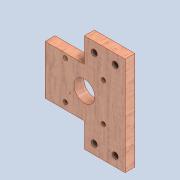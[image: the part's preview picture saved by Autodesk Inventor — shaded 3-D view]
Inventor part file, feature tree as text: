
AUTODESK INVENTOR PART (.ipt)
format: ipt  version: 2020 (Build 240168000, 168)  size: 169,472 bytes
history: native  units: mm
features: sketch x4, extrude x3, hole x1, pattern_linear x1
ambient origin geometry x8: Origin, YZ Plane, XZ Plane, XY Plane, X Axis, Y Axis, Z Axis, Center Point
bodies: Solid1 (feature_tree)
feature tree (9):
  extrude  "Extrusion1"  Depth=40.0mm
  extrude  "Extrusion5"  Depth=20.0mm
  extrude  "Extrusion6"  Depth=33.0mm
  hole  "Hole1"  [1 undecoded]
  pattern_linear  "Rectangular Pattern1"  Spacing1=33.0mm  [1 undecoded]
  sketch  "Sketch1"  dims[d0=65.0mm d1=40.0mm]
  sketch  "Sketch5"  dims[d2=8.0mm d3=0.0mm d22=20.0mm]
  sketch  "Sketch6"  dims[d23=20.0mm d24=33.0mm]
  sketch  "Sketch7"  dims[d25=10.0mm d26=0.0mm d29=31.0mm d30=33.0mm d31=39.0mm d32=3.5mm d33=17.0mm d34=10.0mm d35=0.0mm d36=8.0mm d37=8.0mm d38=8.0mm d39=17.0mm d40=8.0mm d41=64.0mm d42=5.0mm d43=6.0mm d44=4.0mm d45=2.0mm d46=90.0deg d47=8.0mm d48=20.594885mm d49=20.0mm d51=64.0mm d52=20.0mm d54=17.0mm]
note: 2 required parameter values undecoded (feature->parameter linkage not recoverable at this tier; creation-order binding heuristic only, values carry confidence <= 0.55)
